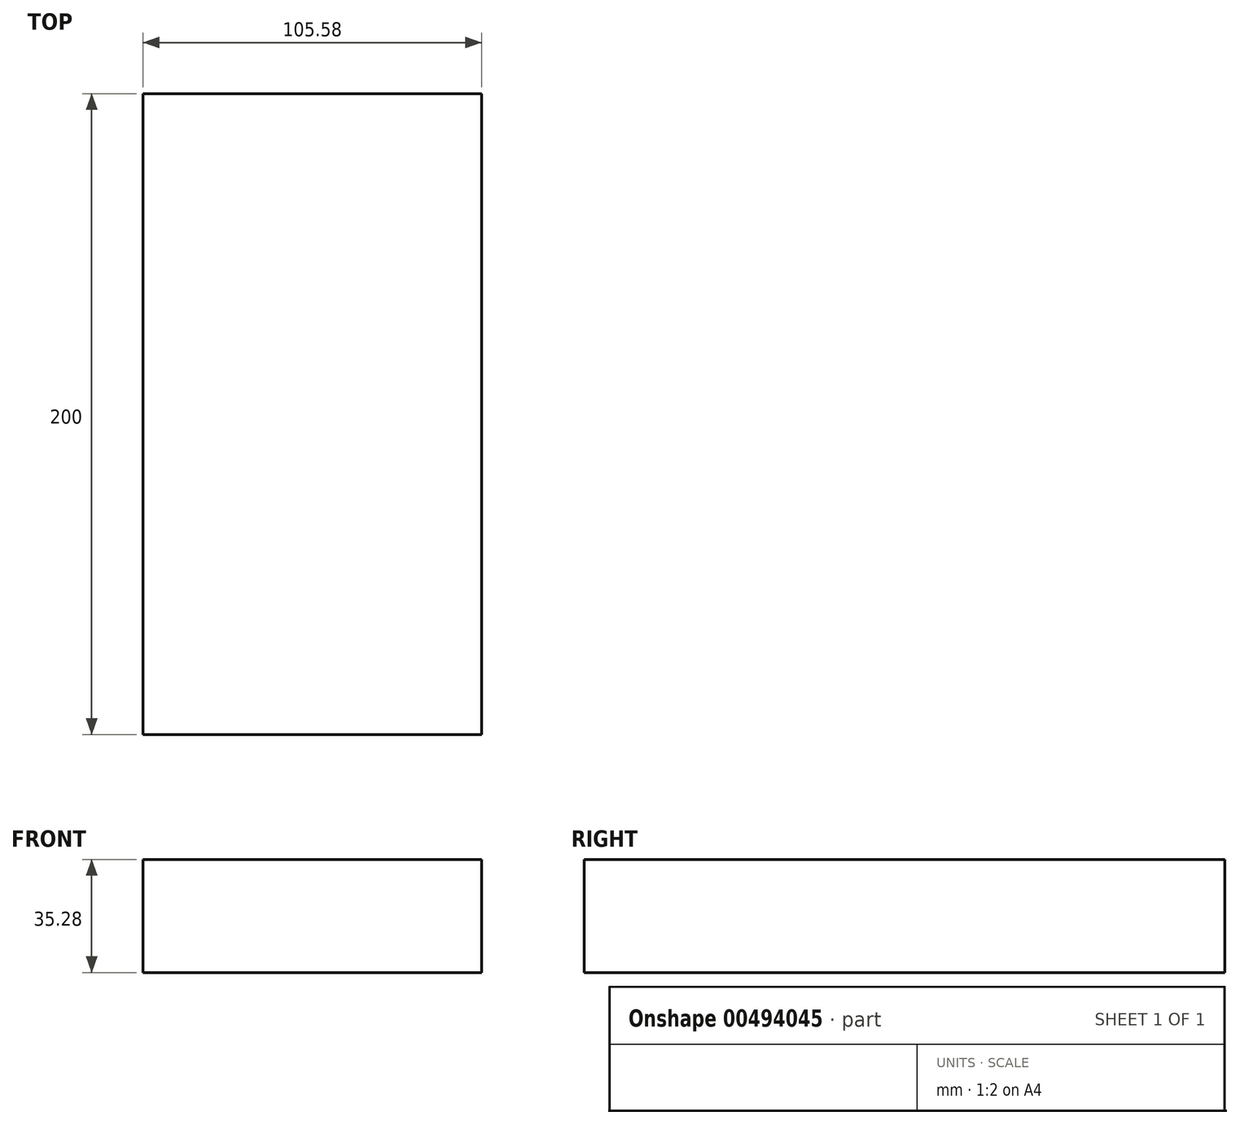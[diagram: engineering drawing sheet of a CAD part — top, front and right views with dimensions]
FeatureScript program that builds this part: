
annotation { "Feature Type Name" : "Feature", "Feature Type Description" : "" }
export const myFeature = defineFeature(function(context is Context, id is Id, definition is map)
    precondition{}
    {
        {
            var Q0;
            Q0=qCreatedBy(makeId("Front.planeOp"),FACE);
            var sketch = newSketch(context, id + "F0", { "sketchPlane" : qUnion([Q0])});
            skLineSegment(sketch, "E0.bottom", {"start": v(52.79, 17.64) * mm, "end": v(-52.79, 17.64) * mm});
            skLineSegment(sketch, "E0.top", {"start": v(52.79, -17.64) * mm, "end": v(-52.79, -17.64) * mm});
            skLineSegment(sketch, "E0.left", {"start": v(52.79, 17.64) * mm, "end": v(52.79, -17.64) * mm});
            skLineSegment(sketch, "E0.right", {"start": v(-52.79, 17.64) * mm, "end": v(-52.79, -17.64) * mm});
            skPoint(sketch, "E0.middle", {"position": v(0, 0) * mm});
            skSolve(sketch);
        }
        {
            var Q0;
            Q0=makeQuery(id+"F0.imprint","IMPRINT",FACE,{"disambiguationData":[TD([[makeQuery(id+"F0.imprint","IMPRINT",EDGE,{"derivedFrom":sQuery(id+"F0.wireOp",EDGE,"E0.bottom")}),1.0]])]});
            extrude(context, id + "F1", {"entities" : qUnion([Q0]), "depth" : 200 * mm});
        }
    });
